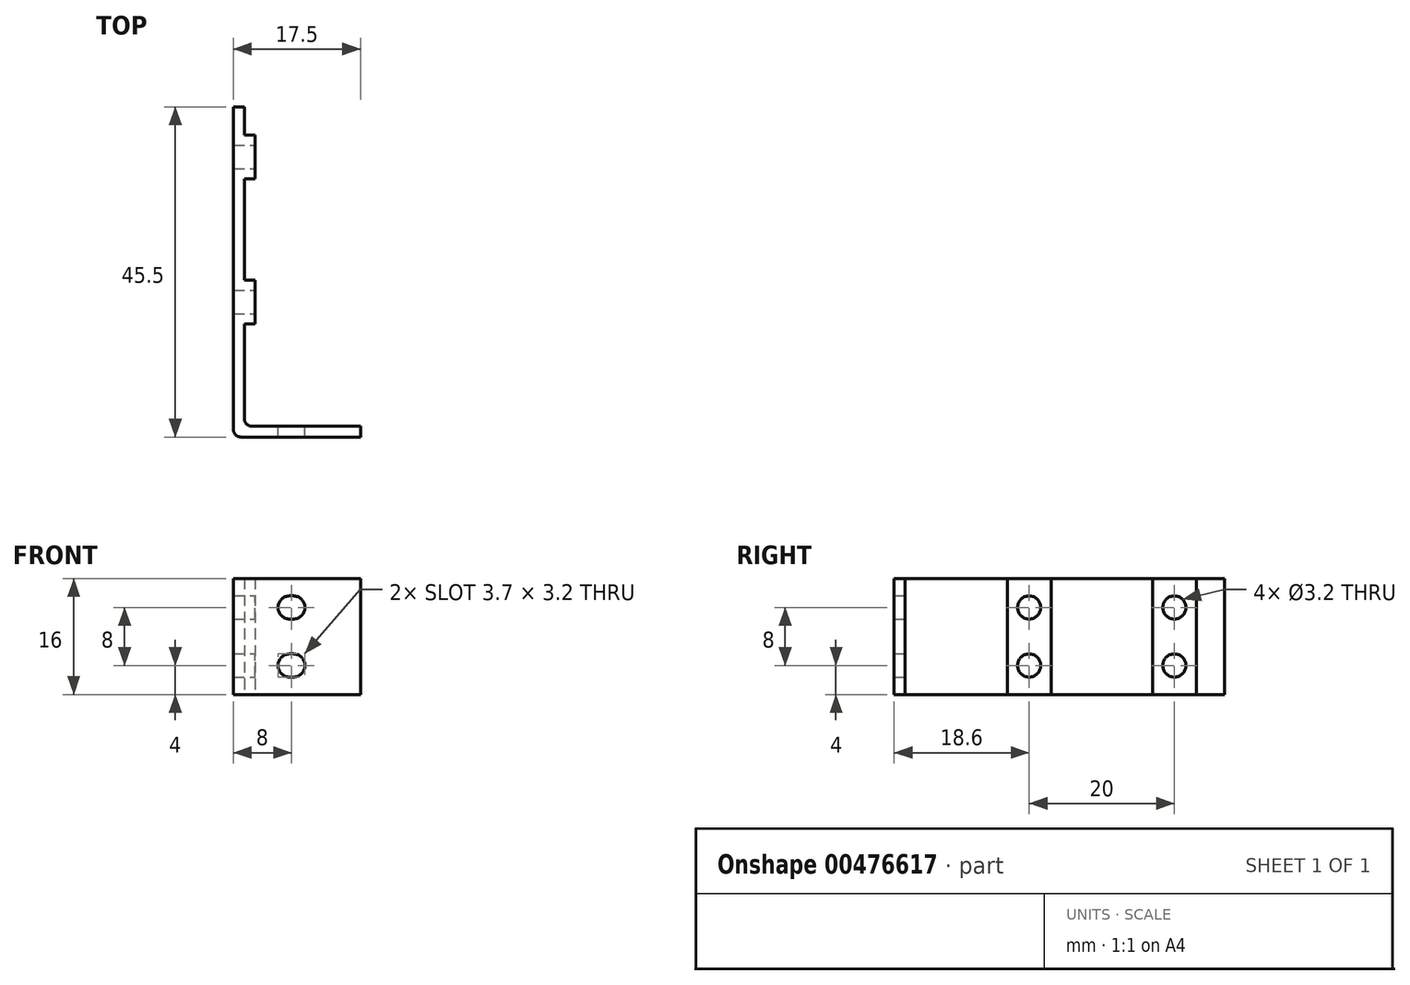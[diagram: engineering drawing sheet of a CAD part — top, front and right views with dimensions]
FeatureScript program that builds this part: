
annotation { "Feature Type Name" : "Feature", "Feature Type Description" : "" }
export const myFeature = defineFeature(function(context is Context, id is Id, definition is map)
    precondition{}
    {
        {
            var Q0;
            Q0=qCreatedBy(makeId("Top.planeOp"),FACE);
            var sketch = newSketch(context, id + "F0", { "sketchPlane" : qUnion([Q0])});
            skLineSegment(sketch, "E0", {"start": v(0, 45.5) * mm, "end": v(-1.5, 45.5) * mm});
            skLineSegment(sketch, "E1", {"start": v(-1.5, 45.5) * mm, "end": v(-1.5, 0) * mm});
            skLineSegment(sketch, "E2", {"start": v(-1.5, 0) * mm, "end": v(16, 0) * mm});
            skLineSegment(sketch, "E3", {"start": v(16, 0) * mm, "end": v(16, 1.5) * mm});
            skLineSegment(sketch, "E4", {"start": v(16, 1.5) * mm, "end": v(0, 1.5) * mm});
            skLineSegment(sketch, "E5", {"start": v(0, 1.5) * mm, "end": v(0, 45.5) * mm});
            skSolve(sketch);
        }
        {
            var Q0;
            Q0 = qSketchRegion(id + "F0", true);
            extrude(context, id + "F1", {"entities" : qUnion([Q0]), "depth" : 16 * mm});
        }
        {
            var Q0;
            Q0=makeQuery(id+"F1.opExtrude","SWEPT_EDGE",EDGE,{"disambiguationData":[OSD([sQuery(id+"F0.wireOp",EDGE,"E1"),sQuery(id+"F0.wireOp",EDGE,"E2")])]});
            fillet(context, id + "F2", {"entities" : qUnion([Q0]), "radius" : 1 * mm, "tangentPropagation" : true, "allowEdgeOverflow" : false});
        }
        {
            var Q0;
            Q0=makeQuery(id+"F1.opExtrude","SWEPT_EDGE",EDGE,{"disambiguationData":[OSD([sQuery(id+"F0.wireOp",EDGE,"E4"),sQuery(id+"F0.wireOp",EDGE,"E5")])]});
            fillet(context, id + "F3", {"entities" : qUnion([Q0]), "radius" : 1 * mm, "tangentPropagation" : true, "allowEdgeOverflow" : false});
        }
        {
            var Q0;
            Q0=makeQuery(id+"F1.opExtrude","SWEPT_FACE",FACE,{"disambiguationData":[OSD([sQuery(id+"F0.wireOp",EDGE,"E4")])]});
            var sketch = newSketch(context, id + "F4", { "sketchPlane" : qUnion([Q0])});
            skLineSegment(sketch, "E6.bottom", {"start": v(-6.75, 2.4) * mm, "end": v(-6.25, 2.4) * mm});
            skLineSegment(sketch, "E6.top", {"start": v(-6.75, 5.6) * mm, "end": v(-6.25, 5.6) * mm});
            skPoint(sketch, "E6.middle", {"position": v(-6.5, 4) * mm});
            skArc(sketch, "E7", {"start": v(-6.75, 5.6) * mm, "mid": v(-8.35, 4) * mm, "end": v(-6.75, 2.4) * mm});
            skArc(sketch, "E8", {"start": v(-6.25, 2.4) * mm, "mid": v(-4.65, 4) * mm, "end": v(-6.25, 5.6) * mm});
            skLineSegment(sketch, "E9.bottom", {"start": v(-6.75, 10.4) * mm, "end": v(-6.25, 10.4) * mm});
            skLineSegment(sketch, "E9.top", {"start": v(-6.75, 13.6) * mm, "end": v(-6.25, 13.6) * mm});
            skPoint(sketch, "E9.middle", {"position": v(-6.5, 12) * mm});
            skArc(sketch, "E10", {"start": v(-6.75, 13.6) * mm, "mid": v(-8.35, 12) * mm, "end": v(-6.75, 10.4) * mm});
            skArc(sketch, "E11", {"start": v(-6.25, 10.4) * mm, "mid": v(-4.65, 12) * mm, "end": v(-6.25, 13.6) * mm});
            skSolve(sketch);
        }
        {
            var Q0;
            Q0 = qSketchRegion(id + "F4", true);
            extrude(context, id + "F5", {"entities" : qUnion([Q0]), "operationType" : NewBodyOperationType.REMOVE, "oppositeDirection" : true, "depth" : 1.5 * mm});
        }
        {
            var Q0;
            Q0=makeQuery(id+"F1.opExtrude","SWEPT_FACE",FACE,{"disambiguationData":[OSD([sQuery(id+"F0.wireOp",EDGE,"E5")])]});
            var sketch = newSketch(context, id + "F6", { "sketchPlane" : qUnion([Q0])});
            skLineSegment(sketch, "E12.bottom", {"start": v(35.6, 16) * mm, "end": v(41.6, 16) * mm});
            skLineSegment(sketch, "E12.top", {"start": v(35.6, 0) * mm, "end": v(41.6, 0) * mm});
            skLineSegment(sketch, "E12.left", {"start": v(35.6, 16) * mm, "end": v(35.6, 0) * mm});
            skLineSegment(sketch, "E12.right", {"start": v(41.6, 16) * mm, "end": v(41.6, 0) * mm});
            skLineSegment(sketch, "E13.bottom", {"start": v(15.6, 16) * mm, "end": v(21.6, 16) * mm});
            skLineSegment(sketch, "E13.top", {"start": v(15.6, 0) * mm, "end": v(21.6, 0) * mm});
            skLineSegment(sketch, "E13.left", {"start": v(15.6, 16) * mm, "end": v(15.6, 0) * mm});
            skLineSegment(sketch, "E13.right", {"start": v(21.6, 16) * mm, "end": v(21.6, 0) * mm});
            skSolve(sketch);
        }
        {
            var Q0;
            Q0 = qSketchRegion(id + "F6", true);
            extrude(context, id + "F7", {"entities" : qUnion([Q0]), "operationType" : NewBodyOperationType.ADD, "depth" : 1.5 * mm});
        }
        {
            var Q0;
            Q0=makeQuery(id+"F7.opExtrude","CAP_FACE",FACE,{"disambiguationData":[OSD([sQuery(id+"F6.wireOp",EDGE,"E12.bottom"),sQuery(id+"F6.wireOp",EDGE,"E12.top"),sQuery(id+"F6.wireOp",EDGE,"E12.left"),sQuery(id+"F6.wireOp",EDGE,"E12.right")])],"isStart":false});
            var sketch = newSketch(context, id + "F8", { "sketchPlane" : qUnion([Q0])});
            skCircle(sketch, "E14", {"center": v(38.6, 12) * mm, "radius": 1.6 * mm});
            skCircle(sketch, "E15", {"center": v(38.6, 4) * mm, "radius": 1.6 * mm});
            skCircle(sketch, "E16", {"center": v(18.6, 12) * mm, "radius": 1.6 * mm});
            skCircle(sketch, "E17", {"center": v(18.6, 4) * mm, "radius": 1.6 * mm});
            skSolve(sketch);
        }
        {
            var Q0;
            Q0 = qSketchRegion(id + "F8", true);
            extrude(context, id + "F9", {"entities" : qUnion([Q0]), "operationType" : NewBodyOperationType.REMOVE, "oppositeDirection" : true, "depth" : 3 * mm});
        }
    });
